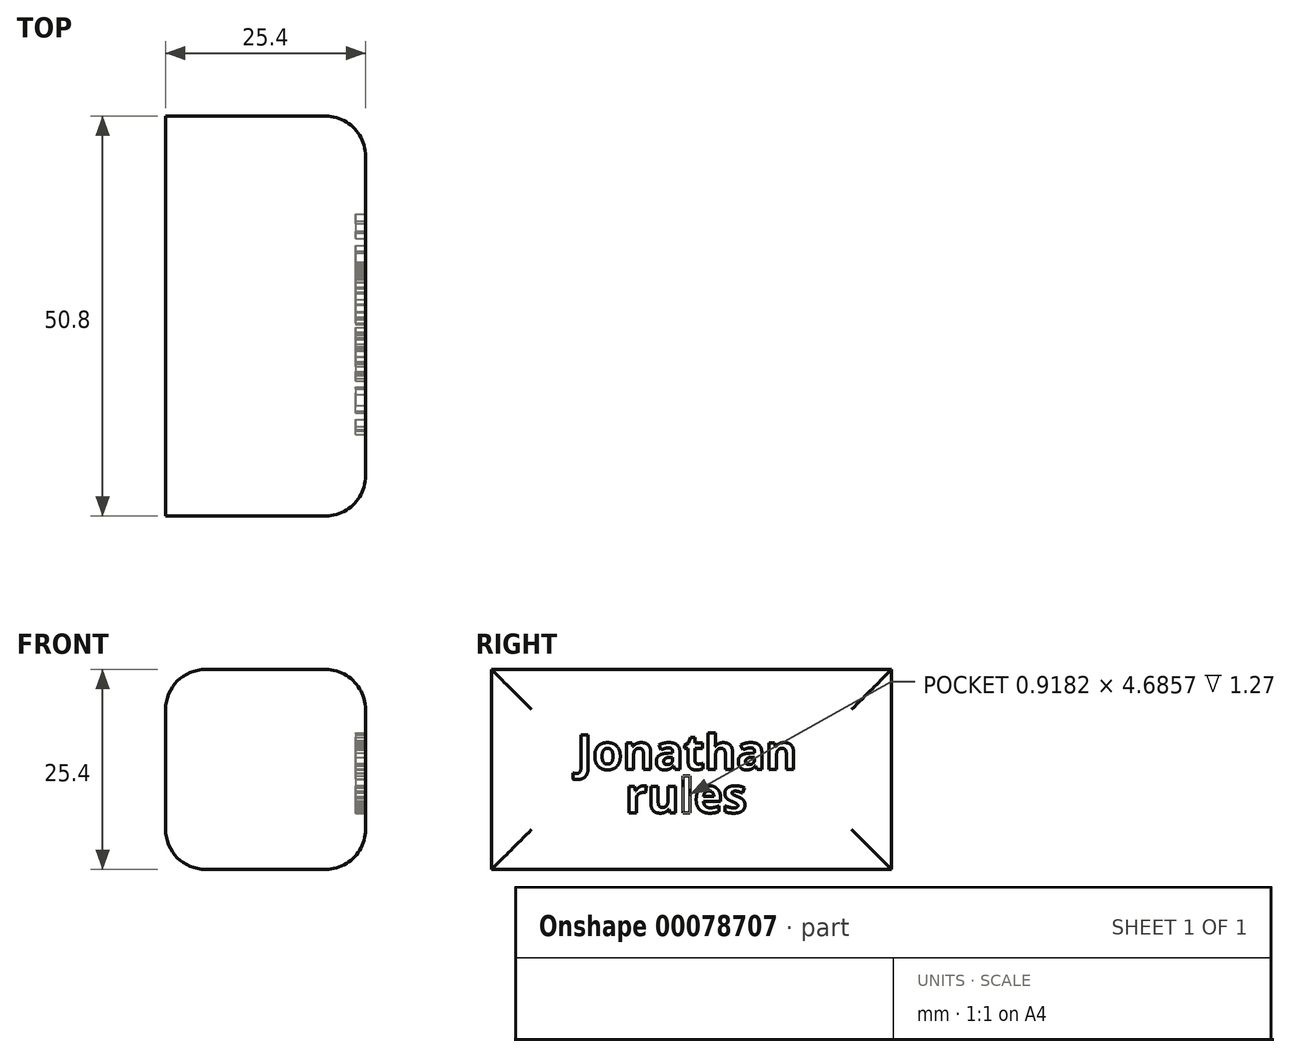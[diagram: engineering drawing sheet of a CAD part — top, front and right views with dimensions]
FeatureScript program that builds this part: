
annotation { "Feature Type Name" : "Feature", "Feature Type Description" : "" }
export const myFeature = defineFeature(function(context is Context, id is Id, definition is map)
    precondition{}
    {
        {
            var Q0;
            Q0=qCreatedBy(makeId("Front.planeOp"),FACE);
            var sketch = newSketch(context, id + "F0", { "sketchPlane" : qUnion([Q0])});
            skLineSegment(sketch, "E0.bottom", {"start": v(12.7, 12.7) * mm, "end": v(-12.7, 12.7) * mm});
            skLineSegment(sketch, "E0.top", {"start": v(12.7, -12.7) * mm, "end": v(-12.7, -12.7) * mm});
            skLineSegment(sketch, "E0.left", {"start": v(12.7, 12.7) * mm, "end": v(12.7, -12.7) * mm});
            skLineSegment(sketch, "E0.right", {"start": v(-12.7, 12.7) * mm, "end": v(-12.7, -12.7) * mm});
            skPoint(sketch, "E0.middle", {"position": v(0, 0) * mm});
            skSolve(sketch);
        }
        {
            var Q0;
            Q0 = qSketchRegion(id + "F0", true);
            extrude(context, id + "F1", {"entities" : qUnion([Q0]), "depth" : 50.8 * mm});
        }
        {
            var Q0;
            Q0=makeQuery(id+"F1.opExtrude","SWEPT_EDGE",EDGE,{"disambiguationData":[OSD([sQuery(id+"F0.wireOp",EDGE,"E0.bottom"),sQuery(id+"F0.wireOp",EDGE,"E0.left")])]});
            var Q1;
            Q1=makeQuery(id+"F1.opExtrude","SWEPT_EDGE",EDGE,{"disambiguationData":[OSD([sQuery(id+"F0.wireOp",EDGE,"E0.bottom"),sQuery(id+"F0.wireOp",EDGE,"E0.right")])]});
            var Q2;
            Q2=makeQuery(id+"F1.opExtrude","SWEPT_EDGE",EDGE,{"disambiguationData":[OSD([sQuery(id+"F0.wireOp",EDGE,"E0.top"),sQuery(id+"F0.wireOp",EDGE,"E0.left")])]});
            var Q3;
            Q3=makeQuery(id+"F1.opExtrude","SWEPT_EDGE",EDGE,{"disambiguationData":[OSD([sQuery(id+"F0.wireOp",EDGE,"E0.top"),sQuery(id+"F0.wireOp",EDGE,"E0.right")])]});
            fillet(context, id + "F2", {"entities" : qUnion([Q0, Q1, Q2, Q3]), "radius" : 5.08 * mm, "tangentPropagation" : true, "allowEdgeOverflow" : false});
        }
        {
            var Q0;
            Q0=makeQuery(id+"F1.opExtrude","CAP_EDGE",EDGE,{"disambiguationData":[OSD([sQuery(id+"F0.wireOp",EDGE,"E0.left")])],"isStart":false});
            var Q1;
            Q1=makeQuery(id+"F1.opExtrude","CAP_EDGE",EDGE,{"disambiguationData":[OSD([sQuery(id+"F0.wireOp",EDGE,"E0.left")])],"isStart":true});
            fillet(context, id + "F3", {"entities" : qUnion([Q0, Q1]), "radius" : 5.08 * mm, "allowEdgeOverflow" : false});
        }
        {
            var Q0;
            Q0=makeQuery(id+"F1.opExtrude","SWEPT_FACE",FACE,{"disambiguationData":[OSD([sQuery(id+"F0.wireOp",EDGE,"E0.left")])]});
            var sketch = newSketch(context, id + "F4", { "sketchPlane" : qUnion([Q0])});
            skText(sketch, "E1", { "text": "Jonathan\n", "fontName": "OpenSans-Bold.ttf"});
            skText(sketch, "E2", { "text": "rules\n", "fontName": "OpenSans-Bold.ttf"});
            const initialGuessF4  = {"E1": [-0.04, 0, 1, 0, 0.00442], "E2": [-0.03382, -0.0055, 1, 0, 0.00444]};
            skSetInitialGuess(sketch, initialGuessF4);
            skSolve(sketch);
        }
        {
            var Q0;
            Q0 = qSketchRegion(id + "F4", true);
            extrude(context, id + "F5", {"entities" : qUnion([Q0]), "operationType" : NewBodyOperationType.REMOVE, "oppositeDirection" : true, "depth" : 1.27 * mm});
        }
    });
